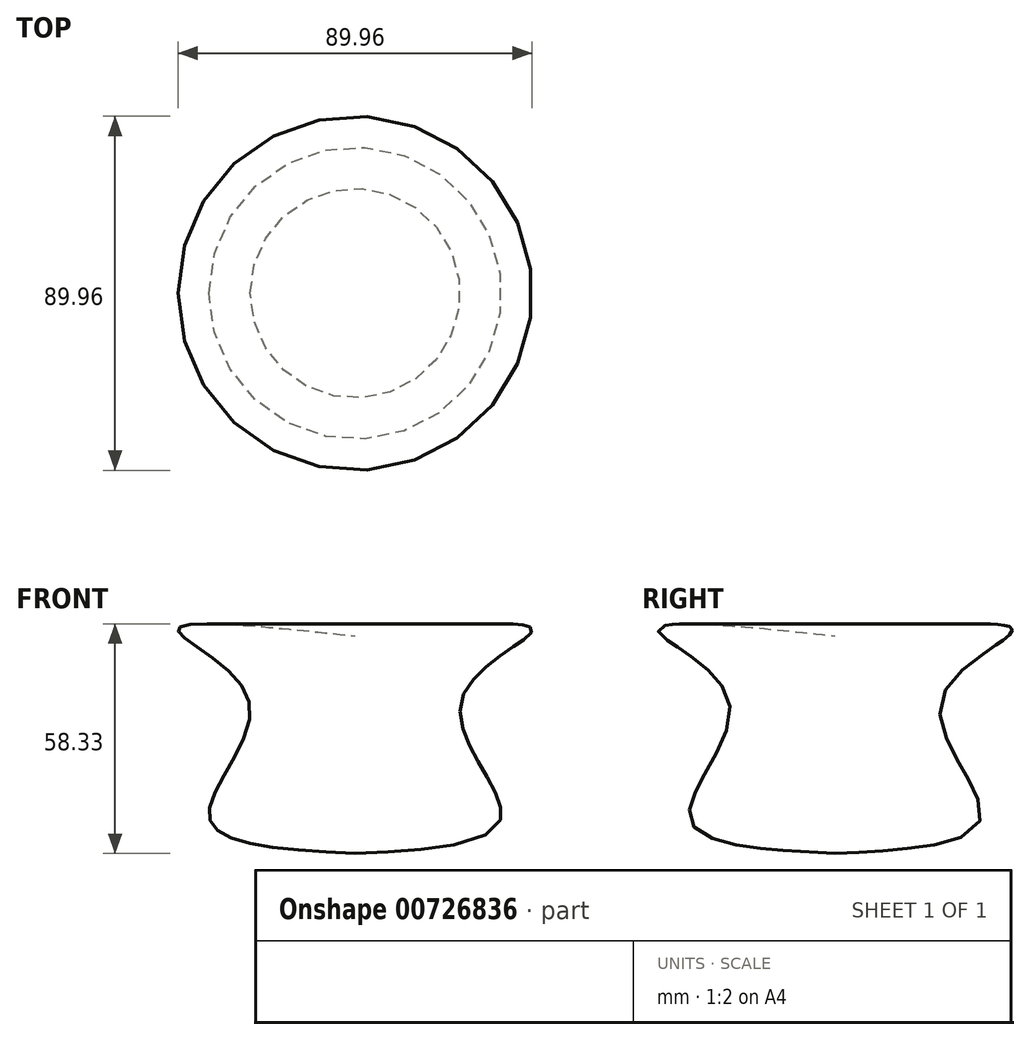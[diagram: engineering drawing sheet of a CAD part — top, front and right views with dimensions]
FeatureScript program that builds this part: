
annotation { "Feature Type Name" : "Feature", "Feature Type Description" : "" }
export const myFeature = defineFeature(function(context is Context, id is Id, definition is map)
    precondition{}
    {
        {
            var Q0;
            Q0=qCreatedBy(makeId("Front.planeOp"),FACE);
            var sketch = newSketch(context, id + "F0", { "sketchPlane" : qUnion([Q0])});
            skFitSpline(sketch, "E0", {"points": [v(0, 0) * mm, v(-37.1, 9.48) * mm, v(-26.9, 38.64) * mm, v(-44.92, 56.42) * mm, v(0, 55.24) * mm], "startDerivative": vector(-206.54, 9.72) * mm, "endDerivative": vector(243.33, -25.81) * mm});
            skLineSegment(sketch, "E1", {"start": v(0, 55.24) * mm, "end": v(0, 0) * mm});
            skSolve(sketch);
        }
        {
            var Q0;
            Q0=makeQuery(id+"F0.imprint","IMPRINT",FACE,{"disambiguationData":[TD([[makeQuery(id+"F0.imprint","IMPRINT",EDGE,{"derivedFrom":sQuery(id+"F0.wireOp",EDGE,"E0")}),-1.0]])]});
            var Q1;
            Q1=sQuery(id+"F0.wireOp",EDGE,"E1");
            revolve(context, id + "F1", {"surfaceOperationType" : NewSurfaceOperationType.NEW, "entities" : qUnion([Q0]), "axis" : qUnion([Q1]), "revolveType" : RevolveType.FULL});
        }
    });
